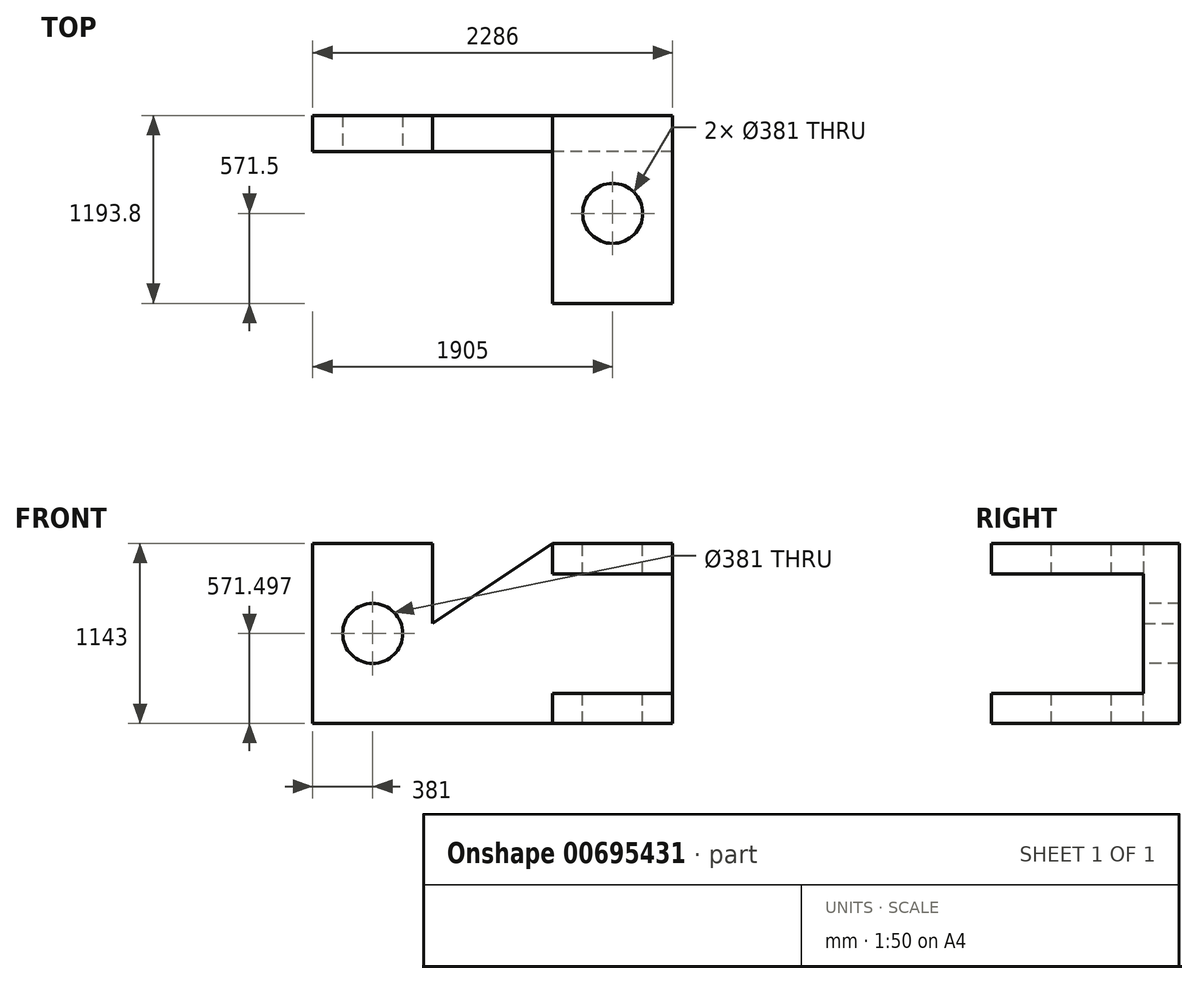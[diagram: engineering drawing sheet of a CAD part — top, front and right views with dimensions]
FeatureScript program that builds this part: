
annotation { "Feature Type Name" : "Feature", "Feature Type Description" : "" }
export const myFeature = defineFeature(function(context is Context, id is Id, definition is map)
    precondition{}
    {
        {
            var Q0;
            Q0=qCreatedBy(makeId("Front.planeOp"),FACE);
            var sketch = newSketch(context, id + "F0", { "sketchPlane" : qUnion([Q0])});
            skLineSegment(sketch, "E0", {"start": v(-1328.47, 324.59) * mm, "end": v(-566.47, 324.59) * mm});
            skLineSegment(sketch, "E1", {"start": v(-1328.47, 324.59) * mm, "end": v(-1328.47, -818.41) * mm});
            skLineSegment(sketch, "E2", {"start": v(-1328.47, -818.41) * mm, "end": v(957.53, -818.41) * mm});
            skLineSegment(sketch, "E3", {"start": v(957.53, -818.41) * mm, "end": v(957.53, 324.59) * mm});
            skLineSegment(sketch, "E4", {"start": v(957.53, 324.59) * mm, "end": v(195.53, 324.59) * mm});
            skLineSegment(sketch, "E5", {"start": v(-566.47, 324.59) * mm, "end": v(-566.47, -183.41) * mm});
            skLineSegment(sketch, "E6", {"start": v(195.53, 324.59) * mm, "end": v(-566.47, -183.41) * mm});
            skSolve(sketch);
        }
        {
            var Q0;
            Q0=makeQuery(id+"F0.imprint","IMPRINT",FACE,{"disambiguationData":[TD([[makeQuery(id+"F0.imprint","IMPRINT",EDGE,{"derivedFrom":sQuery(id+"F0.wireOp",EDGE,"E0")}),-1.0]])]});
            extrude(context, id + "F1", {"entities" : qUnion([Q0]), "depth" : 25.4 * mm, "offsetDistance" : 25.4 * mm});
        }
        {
            var Q0;
            Q0=makeQuery(id+"F1.opExtrude","CAP_FACE",FACE,{"disambiguationData":[OSD([sQuery(id+"F0.wireOp",EDGE,"E0"),sQuery(id+"F0.wireOp",EDGE,"E1"),sQuery(id+"F0.wireOp",EDGE,"E2"),sQuery(id+"F0.wireOp",EDGE,"E3"),sQuery(id+"F0.wireOp",EDGE,"E4"),sQuery(id+"F0.wireOp",EDGE,"E5"),sQuery(id+"F0.wireOp",EDGE,"E6")])],"isStart":false});
            extrude(context, id + "F2", {"entities" : qUnion([Q0]), "operationType" : NewBodyOperationType.ADD, "depth" : 203.2 * mm, "offsetDistance" : 25.4 * mm});
        }
        {
            var Q0;
            Q0=makeQuery(id+"F2.opExtrude","CAP_FACE",FACE,{"disambiguationData":[OSD([sQuery(id+"F0.wireOp",EDGE,"E0"),sQuery(id+"F0.wireOp",EDGE,"E1"),sQuery(id+"F0.wireOp",EDGE,"E2"),sQuery(id+"F0.wireOp",EDGE,"E3"),sQuery(id+"F0.wireOp",EDGE,"E4"),sQuery(id+"F0.wireOp",EDGE,"E5"),sQuery(id+"F0.wireOp",EDGE,"E6")])],"isStart":false});
            var sketch = newSketch(context, id + "F3", { "sketchPlane" : qUnion([Q0])});
            skLineSegment(sketch, "E7.bottom", {"start": v(195.53, 324.59) * mm, "end": v(957.53, 324.59) * mm});
            skLineSegment(sketch, "E7.top", {"start": v(195.53, 130.76) * mm, "end": v(957.53, 130.76) * mm});
            skLineSegment(sketch, "E7.left", {"start": v(195.53, 324.59) * mm, "end": v(195.53, 130.76) * mm});
            skLineSegment(sketch, "E7.right", {"start": v(957.53, 324.59) * mm, "end": v(957.53, 130.76) * mm});
            skLineSegment(sketch, "E8.bottom", {"start": v(957.53, -818.41) * mm, "end": v(195.53, -818.41) * mm});
            skLineSegment(sketch, "E8.top", {"start": v(957.53, -626.53) * mm, "end": v(195.53, -626.53) * mm});
            skLineSegment(sketch, "E8.left", {"start": v(957.53, -818.41) * mm, "end": v(957.53, -626.53) * mm});
            skLineSegment(sketch, "E8.right", {"start": v(195.53, -818.41) * mm, "end": v(195.53, -626.53) * mm});
            skSolve(sketch);
        }
        {
            var Q0;
            Q0=makeQuery(id+"F3.imprint","IMPRINT",FACE,{"disambiguationData":[TD([[makeQuery(id+"F3.imprint","IMPRINT",EDGE,{"derivedFrom":sQuery(id+"F3.wireOp",EDGE,"E7.bottom")}),1.0]])]});
            var Q1;
            Q1=makeQuery(id+"F3.imprint","IMPRINT",FACE,{"disambiguationData":[TD([[makeQuery(id+"F3.imprint","IMPRINT",EDGE,{"derivedFrom":sQuery(id+"F3.wireOp",EDGE,"E8.bottom")}),1.0]])]});
            extrude(context, id + "F4", {"entities" : qUnion([Q0, Q1]), "operationType" : NewBodyOperationType.ADD, "depth" : 965.2 * mm, "offsetDistance" : 25.4 * mm});
        }
        {
            var Q0;
            {var subQ0=sQuery(id+"F0.wireOp",EDGE,"E4");Q0=makeQuery(id+"F4.boolean.opBoolean","MERGE",FACE,{"derivedFrom":[makeQuery(id+"F2.boolean.opBoolean","MERGE",FACE,{"derivedFrom":[makeQuery(id+"F1.opExtrude","SWEPT_FACE",FACE,{"disambiguationData":[OSD([subQ0])]}),makeQuery(id+"F2.opExtrude","SWEPT_FACE",FACE,{"disambiguationData":[OSD([subQ0])]})]}),makeQuery(id+"F4.opExtrude","SWEPT_FACE",FACE,{"disambiguationData":[OSD([sQuery(id+"F3.wireOp",EDGE,"E7.bottom")])]})]});}
            var sketch = newSketch(context, id + "F5", { "sketchPlane" : qUnion([Q0])});
            skCircle(sketch, "E9", {"center": v(576.53, -622.3) * mm, "radius": 190.5 * mm});
            skSolve(sketch);
        }
        {
            var Q0;
            Q0=makeQuery(id+"F4.opExtrude","SWEPT_FACE",FACE,{"disambiguationData":[OSD([sQuery(id+"F3.wireOp",EDGE,"E8.top")])]});
            var sketch = newSketch(context, id + "F6", { "sketchPlane" : qUnion([Q0])});
            skCircle(sketch, "E10", {"center": v(576.53, -622.3) * mm, "radius": 190.5 * mm});
            skSolve(sketch);
        }
        {
            var Q0;
            Q0=sQuery(id+"F5.wireOp",VERTEX,"E9.center");
            var Q1;
            Q1=sQuery(id+"F6.wireOp",VERTEX,"E10.center");
            var Q2;
            Q2=makeQuery(id+"F1.opExtrude","SWEPT_BODY",BODY,{"disambiguationData":[OSD([sQuery(id+"F0.wireOp",EDGE,"E0"),sQuery(id+"F0.wireOp",EDGE,"E1"),sQuery(id+"F0.wireOp",EDGE,"E2"),sQuery(id+"F0.wireOp",EDGE,"E3"),sQuery(id+"F0.wireOp",EDGE,"E4"),sQuery(id+"F0.wireOp",EDGE,"E5"),sQuery(id+"F0.wireOp",EDGE,"E6")])]});
            hole(context, id + "F7", {"style" : HoleStyle.SIMPLE, "endStyle" : HoleEndStyle.BLIND, "holeDiameter" : 381 * mm, "majorDiameter" : 6.35 * mm, "holeDepth" : 203.2 * mm, "isTappedThrough" : true, "tappedDepth" : 12.7 * mm, "tapClearance" : 3, "locations" : qUnion([Q0, Q1]), "scope" : qUnion([Q2])});
        }
        {
            var Q0;
            Q0=makeQuery(id+"F2.opExtrude","CAP_FACE",FACE,{"disambiguationData":[OSD([sQuery(id+"F0.wireOp",EDGE,"E0"),sQuery(id+"F0.wireOp",EDGE,"E1"),sQuery(id+"F0.wireOp",EDGE,"E2"),sQuery(id+"F0.wireOp",EDGE,"E3"),sQuery(id+"F0.wireOp",EDGE,"E4"),sQuery(id+"F0.wireOp",EDGE,"E5"),sQuery(id+"F0.wireOp",EDGE,"E6")])],"isStart":false});
            var sketch = newSketch(context, id + "F8", { "sketchPlane" : qUnion([Q0])});
            skCircle(sketch, "E11", {"center": v(-947.47, -246.91) * mm, "radius": 190.5 * mm});
            skSolve(sketch);
        }
        {
            var Q0;
            Q0=sQuery(id+"F8.wireOp",VERTEX,"E11.center");
            var Q1;
            Q1=makeQuery(id+"F1.opExtrude","SWEPT_BODY",BODY,{"disambiguationData":[OSD([sQuery(id+"F0.wireOp",EDGE,"E0"),sQuery(id+"F0.wireOp",EDGE,"E1"),sQuery(id+"F0.wireOp",EDGE,"E2"),sQuery(id+"F0.wireOp",EDGE,"E3"),sQuery(id+"F0.wireOp",EDGE,"E4"),sQuery(id+"F0.wireOp",EDGE,"E5"),sQuery(id+"F0.wireOp",EDGE,"E6")])]});
            hole(context, id + "F9", {"style" : HoleStyle.SIMPLE, "endStyle" : HoleEndStyle.BLIND, "holeDiameter" : 381 * mm, "majorDiameter" : 6.35 * mm, "holeDepth" : 381 * mm, "isTappedThrough" : true, "tappedDepth" : 12.7 * mm, "tapClearance" : 3, "locations" : qUnion([Q0]), "scope" : qUnion([Q1])});
        }
    });
